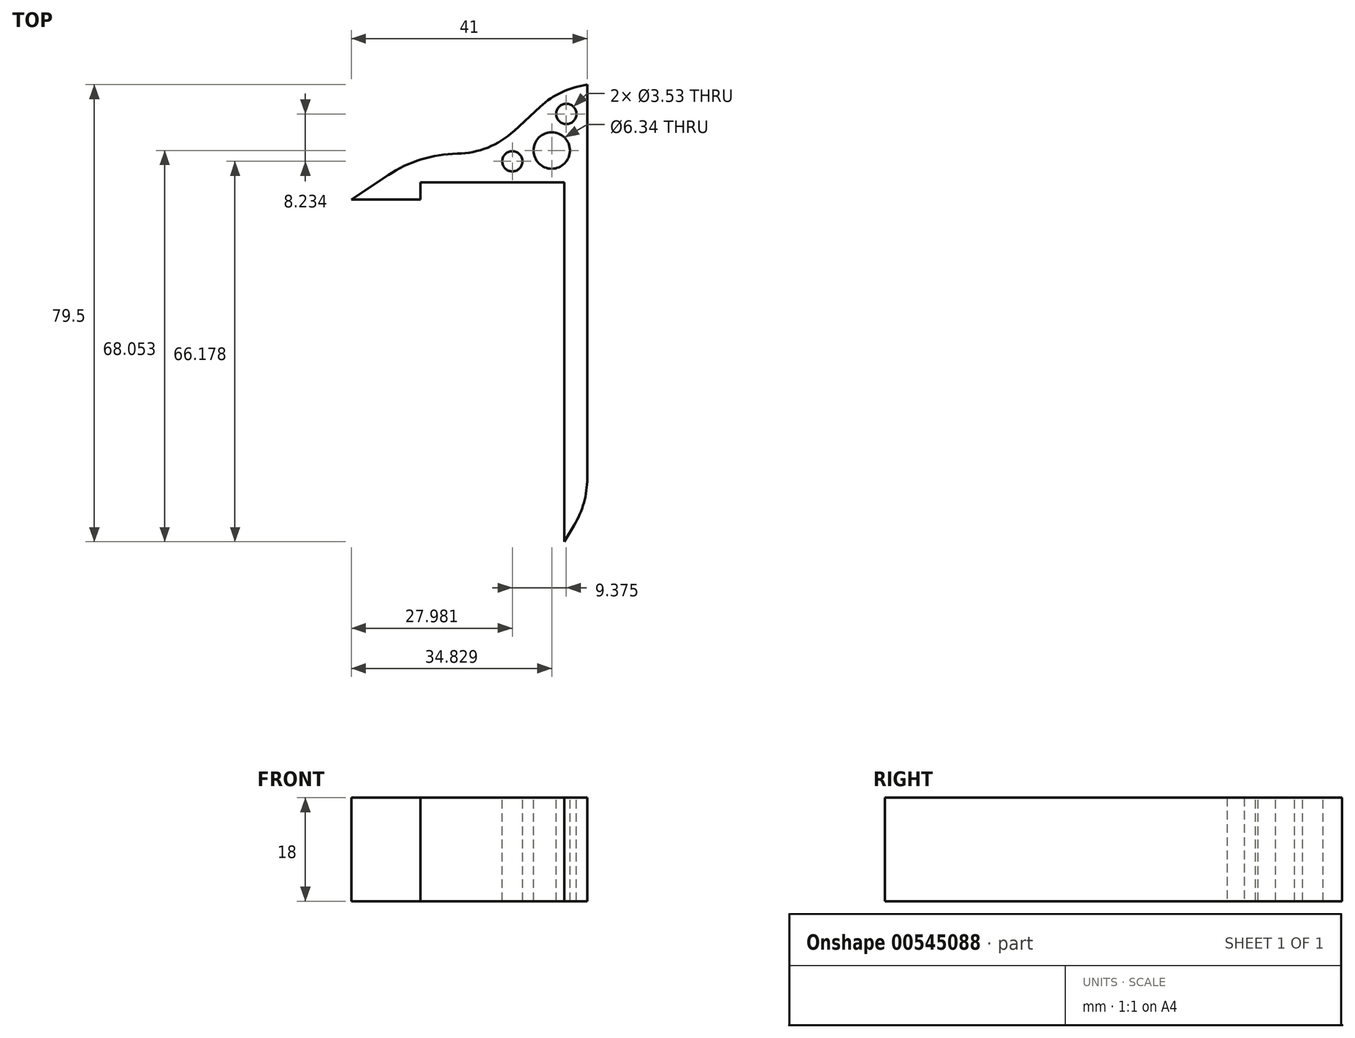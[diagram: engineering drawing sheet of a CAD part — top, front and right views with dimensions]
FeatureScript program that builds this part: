
annotation { "Feature Type Name" : "Feature", "Feature Type Description" : "" }
export const myFeature = defineFeature(function(context is Context, id is Id, definition is map)
    precondition{}
    {
        {
            var Q0;
            Q0=qCreatedBy(makeId("Top.planeOp"),FACE);
            var sketch = newSketch(context, id + "F0", { "sketchPlane" : qUnion([Q0])});
            skLineSegment(sketch, "E0", {"start": v(7.45, 7.6) * mm, "end": v(7.45, -54.9) * mm});
            skLineSegment(sketch, "E1", {"start": v(7.45, 7.6) * mm, "end": v(-17.55, 7.6) * mm});
            skLineSegment(sketch, "E2", {"start": v(-17.55, 7.6) * mm, "end": v(-17.55, 4.6) * mm});
            skLineSegment(sketch, "E3", {"start": v(-17.55, 4.6) * mm, "end": v(-29.55, 4.6) * mm});
            skLineSegment(sketch, "E4", {"start": v(-29.55, 4.6) * mm, "end": v(-17.55, 12.6) * mm});
            skLineSegment(sketch, "E5", {"start": v(-17.55, 12.6) * mm, "end": v(-5.55, 12.6) * mm});
            skLineSegment(sketch, "E6", {"start": v(-5.55, 12.6) * mm, "end": v(7.45, 24.6) * mm});
            skLineSegment(sketch, "E7", {"start": v(7.45, 24.6) * mm, "end": v(11.45, 24.6) * mm});
            skLineSegment(sketch, "E8", {"start": v(11.45, 24.6) * mm, "end": v(11.45, -48.26) * mm});
            skLineSegment(sketch, "E9", {"start": v(11.45, -48.26) * mm, "end": v(7.45, -54.9) * mm});
            skSolve(sketch);
        }
        {
            var Q0;
            Q0=makeQuery(id+"F0.imprint","IMPRINT",FACE,{"disambiguationData":[TD([[makeQuery(id+"F0.imprint","IMPRINT",EDGE,{"derivedFrom":sQuery(id+"F0.wireOp",EDGE,"E0")}),1.0]])]});
            extrude(context, id + "F1", {"entities" : qUnion([Q0]), "depth" : 18 * mm, "offsetDistance" : 25 * mm});
        }
        {
            var Q0;
            Q0=makeQuery(id+"F1.opExtrude","SWEPT_EDGE",EDGE,{"disambiguationData":[OSD([sQuery(id+"F0.wireOp",EDGE,"E5"),sQuery(id+"F0.wireOp",EDGE,"E6")])]});
            var Q1;
            Q1=makeQuery(id+"F1.opExtrude","SWEPT_EDGE",EDGE,{"disambiguationData":[OSD([sQuery(id+"F0.wireOp",EDGE,"E6"),sQuery(id+"F0.wireOp",EDGE,"E7")])]});
            fillet(context, id + "F2", {"entities" : qUnion([Q0, Q1]), "radius" : 14.92 * mm, "tangentPropagation" : true, "allowEdgeOverflow" : false});
        }
        {
            var Q0;
            Q0=makeQuery(id+"F1.opExtrude","SWEPT_EDGE",EDGE,{"disambiguationData":[OSD([sQuery(id+"F0.wireOp",EDGE,"E4"),sQuery(id+"F0.wireOp",EDGE,"E5")])]});
            fillet(context, id + "F3", {"entities" : qUnion([Q0]), "radius" : 22.3 * mm, "tangentPropagation" : true, "allowEdgeOverflow" : false});
        }
        {
            var Q0;
            Q0=makeQuery(id+"F1.opExtrude","SWEPT_EDGE",EDGE,{"disambiguationData":[OSD([sQuery(id+"F0.wireOp",EDGE,"E8"),sQuery(id+"F0.wireOp",EDGE,"E9")])]});
            fillet(context, id + "F4", {"entities" : qUnion([Q0]), "radius" : 15.8 * mm, "tangentPropagation" : true, "allowEdgeOverflow" : false});
        }
        {
            var Q0;
            Q0=makeQuery(id+"F1.opExtrude","CAP_FACE",FACE,{"disambiguationData":[OSD([sQuery(id+"F0.wireOp",EDGE,"E0"),sQuery(id+"F0.wireOp",EDGE,"E1"),sQuery(id+"F0.wireOp",EDGE,"E2"),sQuery(id+"F0.wireOp",EDGE,"E3"),sQuery(id+"F0.wireOp",EDGE,"E4"),sQuery(id+"F0.wireOp",EDGE,"E5"),sQuery(id+"F0.wireOp",EDGE,"E6"),sQuery(id+"F0.wireOp",EDGE,"E7"),sQuery(id+"F0.wireOp",EDGE,"E8"),sQuery(id+"F0.wireOp",EDGE,"E9")])],"isStart":false});
            var sketch = newSketch(context, id + "F5", { "sketchPlane" : qUnion([Q0])});
            skCircle(sketch, "E10", {"center": v(5.28, 13.16) * mm, "radius": 3.17 * mm});
            skCircle(sketch, "E11", {"center": v(-1.57, 11.29) * mm, "radius": 1.76 * mm});
            skCircle(sketch, "E12", {"center": v(7.8, 19.52) * mm, "radius": 1.76 * mm});
            skSolve(sketch);
        }
        {
            var Q0;
            Q0=makeQuery(id+"F5.imprint","IMPRINT",FACE,{"disambiguationData":[TD([[makeQuery(id+"F5.imprint","IMPRINT",EDGE,{"derivedFrom":sQuery(id+"F5.wireOp",EDGE,"E11")}),1.0]])]});
            var Q1;
            Q1=makeQuery(id+"F5.imprint","IMPRINT",FACE,{"disambiguationData":[TD([[makeQuery(id+"F5.imprint","IMPRINT",EDGE,{"derivedFrom":sQuery(id+"F5.wireOp",EDGE,"E10")}),1.0]])]});
            var Q2;
            Q2=makeQuery(id+"F5.imprint","IMPRINT",FACE,{"disambiguationData":[TD([[makeQuery(id+"F5.imprint","IMPRINT",EDGE,{"derivedFrom":sQuery(id+"F5.wireOp",EDGE,"E12")}),1.0]])]});
            extrude(context, id + "F6", {"entities" : qUnion([Q0, Q1, Q2]), "operationType" : NewBodyOperationType.REMOVE, "oppositeDirection" : true, "depth" : 18 * mm, "offsetDistance" : 25 * mm});
        }
    });
